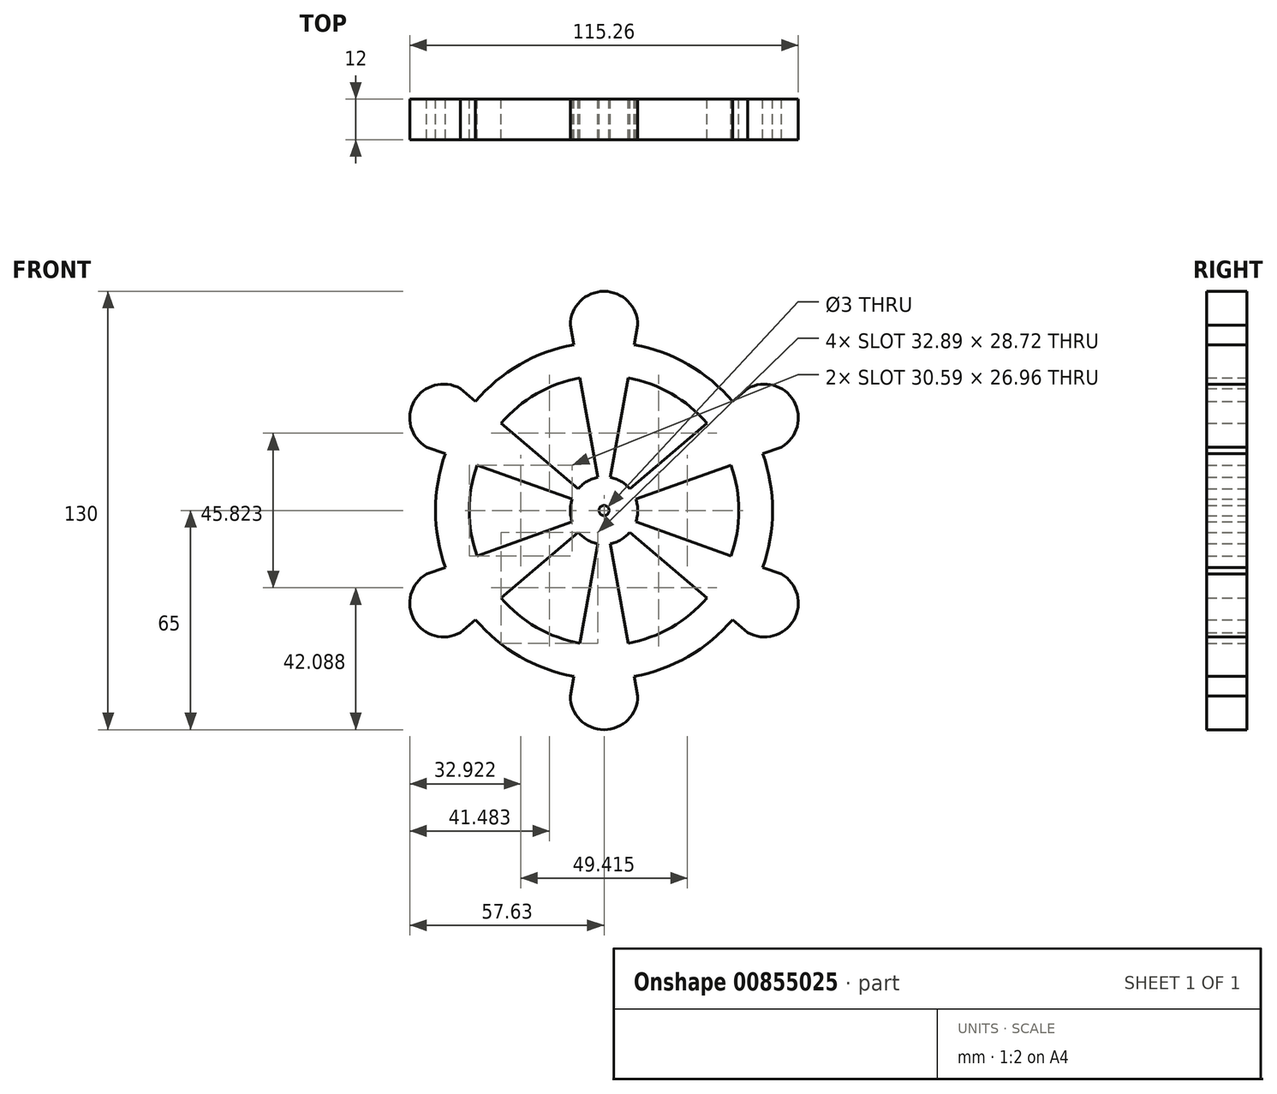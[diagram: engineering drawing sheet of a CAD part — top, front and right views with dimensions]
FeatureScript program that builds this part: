
annotation { "Feature Type Name" : "Feature", "Feature Type Description" : "" }
export const myFeature = defineFeature(function(context is Context, id is Id, definition is map)
    precondition{}
    {
        {
            var Q0;
            Q0=qCreatedBy(makeId("Front.planeOp"),FACE);
            var sketch = newSketch(context, id + "F0", { "sketchPlane" : qUnion([Q0])});
            skArc(sketch, "E0", {"start": v(-0.9, 4.92) * mm, "mid": v(-2.5, 4.33) * mm, "end": v(-3.81, 3.23) * mm});
            skArc(sketch, "E1", {"start": v(-0.72, 3.94) * mm, "mid": v(-2, 3.46) * mm, "end": v(-3.05, 2.59) * mm});
            skCircle(sketch, "E2", {"center": v(0, 0) * mm, "radius": 1 * mm});
            skLineSegment(sketch, "E3", {"start": v(-0.18, 0.98) * mm, "end": v(-1, 5.5) * mm});
            skLineSegment(sketch, "E4", {"start": v(0.18, 0.98) * mm, "end": v(1, 5.5) * mm});
            skArc(sketch, "E5", {"start": v(1, 5.5) * mm, "mid": v(0, 6.5) * mm, "end": v(-1, 5.5) * mm});
            skArc(sketch, "E6.1.0", {"start": v(-4.26, 3.62) * mm, "mid": v(-5.63, 3.25) * mm, "end": v(-5.26, 1.88) * mm});
            skLineSegment(sketch, "E6.1.1", {"start": v(-0.76, 0.65) * mm, "end": v(-4.26, 3.62) * mm});
            skLineSegment(sketch, "E6.1.2", {"start": v(-0.94, 0.34) * mm, "end": v(-5.26, 1.88) * mm});
            skArc(sketch, "E6.2.0", {"start": v(-5.26, -1.88) * mm, "mid": v(-5.63, -3.25) * mm, "end": v(-4.26, -3.62) * mm});
            skLineSegment(sketch, "E6.2.1", {"start": v(-0.94, -0.34) * mm, "end": v(-5.26, -1.88) * mm});
            skLineSegment(sketch, "E6.2.2", {"start": v(-0.76, -0.65) * mm, "end": v(-4.26, -3.62) * mm});
            skArc(sketch, "E6.3.0", {"start": v(-1, -5.5) * mm, "mid": v(0, -6.5) * mm, "end": v(1, -5.5) * mm});
            skLineSegment(sketch, "E6.3.1", {"start": v(-0.18, -0.98) * mm, "end": v(-1, -5.5) * mm});
            skLineSegment(sketch, "E6.3.2", {"start": v(0.18, -0.98) * mm, "end": v(1, -5.5) * mm});
            skArc(sketch, "E6.4.0", {"start": v(4.26, -3.62) * mm, "mid": v(5.63, -3.25) * mm, "end": v(5.26, -1.88) * mm});
            skLineSegment(sketch, "E6.4.1", {"start": v(0.76, -0.65) * mm, "end": v(4.26, -3.62) * mm});
            skLineSegment(sketch, "E6.4.2", {"start": v(0.94, -0.34) * mm, "end": v(5.26, -1.88) * mm});
            skArc(sketch, "E6.5.0", {"start": v(5.26, 1.88) * mm, "mid": v(5.63, 3.25) * mm, "end": v(4.26, 3.62) * mm});
            skLineSegment(sketch, "E6.5.1", {"start": v(0.94, 0.34) * mm, "end": v(5.26, 1.88) * mm});
            skLineSegment(sketch, "E6.5.2", {"start": v(0.76, 0.65) * mm, "end": v(4.26, 3.62) * mm});
            skArc(sketch, "E7.trimOffspring", {"start": v(-4.7, 1.69) * mm, "mid": v(-5, 0) * mm, "end": v(-4.7, -1.69) * mm});
            skArc(sketch, "E8.trimOffspring", {"start": v(-3.77, 1.35) * mm, "mid": v(-4, 0) * mm, "end": v(-3.77, -1.35) * mm});
            skArc(sketch, "E9.trimOffspring", {"start": v(-3.81, -3.23) * mm, "mid": v(-2.5, -4.33) * mm, "end": v(-0.9, -4.92) * mm});
            skArc(sketch, "E10.trimOffspring", {"start": v(-3.05, -2.59) * mm, "mid": v(-2, -3.46) * mm, "end": v(-0.72, -3.94) * mm});
            skArc(sketch, "E11.trimOffspring", {"start": v(0.72, -3.94) * mm, "mid": v(2, -3.46) * mm, "end": v(3.05, -2.59) * mm});
            skArc(sketch, "E12.trimOffspring", {"start": v(0.9, -4.92) * mm, "mid": v(2.5, -4.33) * mm, "end": v(3.81, -3.23) * mm});
            skArc(sketch, "E13.trimOffspring", {"start": v(4.7, -1.69) * mm, "mid": v(5, 0) * mm, "end": v(4.7, 1.69) * mm});
            skArc(sketch, "E14.trimOffspring", {"start": v(3.77, -1.35) * mm, "mid": v(4, 0) * mm, "end": v(3.77, 1.35) * mm});
            skArc(sketch, "E15.trimOffspring", {"start": v(3.05, 2.59) * mm, "mid": v(2, 3.46) * mm, "end": v(0.72, 3.94) * mm});
            skArc(sketch, "E16.trimOffspring", {"start": v(3.81, 3.23) * mm, "mid": v(2.5, 4.33) * mm, "end": v(0.9, 4.92) * mm});
            skSolve(sketch);
        }
        {
            var Q0;
            {var subQ0=sQuery(id+"F0.wireOp",EDGE,"E7.trimOffspring");Q0=makeQuery(id+"F0.imprint","IMPRINT",FACE,{"disambiguationData":[TD([[makeQuery(id+"F0.imprint","IMPRINT",EDGE,{"derivedFrom":subQ0}),1.0]])]});}
            var Q1;
            {var subQ5=sQuery(id+"F0.wireOp",EDGE,"E6.1.0");Q1=makeQuery(id+"F0.imprint","IMPRINT",FACE,{"disambiguationData":[TD([[makeQuery(id+"F0.imprint","IMPRINT",EDGE,{"derivedFrom":subQ5}),1.0]])]});}
            var Q2;
            {var subQ0=sQuery(id+"F0.wireOp",EDGE,"E0");Q2=makeQuery(id+"F0.imprint","IMPRINT",FACE,{"disambiguationData":[TD([[makeQuery(id+"F0.imprint","IMPRINT",EDGE,{"derivedFrom":subQ0}),1.0]])]});}
            var Q3;
            {var subQ2=sQuery(id+"F0.wireOp",EDGE,"E5");Q3=makeQuery(id+"F0.imprint","IMPRINT",FACE,{"disambiguationData":[TD([[makeQuery(id+"F0.imprint","IMPRINT",EDGE,{"derivedFrom":subQ2}),1.0]])]});}
            var Q4;
            {var subQ0=sQuery(id+"F0.wireOp",EDGE,"E15.trimOffspring");Q4=makeQuery(id+"F0.imprint","IMPRINT",FACE,{"disambiguationData":[TD([[makeQuery(id+"F0.imprint","IMPRINT",EDGE,{"derivedFrom":subQ0}),-1.0]])]});}
            var Q5;
            {var subQ5=sQuery(id+"F0.wireOp",EDGE,"E6.5.0");Q5=makeQuery(id+"F0.imprint","IMPRINT",FACE,{"disambiguationData":[TD([[makeQuery(id+"F0.imprint","IMPRINT",EDGE,{"derivedFrom":subQ5}),1.0]])]});}
            var Q6;
            {var subQ0=sQuery(id+"F0.wireOp",EDGE,"E13.trimOffspring");Q6=makeQuery(id+"F0.imprint","IMPRINT",FACE,{"disambiguationData":[TD([[makeQuery(id+"F0.imprint","IMPRINT",EDGE,{"derivedFrom":subQ0}),1.0]])]});}
            var Q7;
            {var subQ5=sQuery(id+"F0.wireOp",EDGE,"E6.4.0");Q7=makeQuery(id+"F0.imprint","IMPRINT",FACE,{"disambiguationData":[TD([[makeQuery(id+"F0.imprint","IMPRINT",EDGE,{"derivedFrom":subQ5}),1.0]])]});}
            var Q8;
            {var subQ0=sQuery(id+"F0.wireOp",EDGE,"E11.trimOffspring");Q8=makeQuery(id+"F0.imprint","IMPRINT",FACE,{"disambiguationData":[TD([[makeQuery(id+"F0.imprint","IMPRINT",EDGE,{"derivedFrom":subQ0}),-1.0]])]});}
            var Q9;
            {var subQ5=sQuery(id+"F0.wireOp",EDGE,"E6.3.0");Q9=makeQuery(id+"F0.imprint","IMPRINT",FACE,{"disambiguationData":[TD([[makeQuery(id+"F0.imprint","IMPRINT",EDGE,{"derivedFrom":subQ5}),1.0]])]});}
            var Q10;
            {var subQ7=sQuery(id+"F0.wireOp",EDGE,"E6.2.0");Q10=makeQuery(id+"F0.imprint","IMPRINT",FACE,{"disambiguationData":[TD([[makeQuery(id+"F0.imprint","IMPRINT",EDGE,{"derivedFrom":subQ7}),1.0]])]});}
            var Q11;
            {var subQ0=sQuery(id+"F0.wireOp",EDGE,"E2");var subQ8=makeQuery(id+"F0.imprint","INTERSECT",VERTEX,{"derivedFrom":[subQ0,sQuery(id+"F0.wireOp",EDGE,"E6.5.1")]});Q11=makeQuery(id+"F0.imprint","IMPRINT",FACE,{"disambiguationData":[TD([[makeQuery(id+"F0.imprint","IMPRINT",EDGE,{"disambiguationData":[TD([[subQ8,-1.0]])],"derivedFrom":subQ0}),1.0]])]});}
            var Q12;
            {var subQ0=sQuery(id+"F0.wireOp",EDGE,"E9.trimOffspring");Q12=makeQuery(id+"F0.imprint","IMPRINT",FACE,{"disambiguationData":[TD([[makeQuery(id+"F0.imprint","IMPRINT",EDGE,{"derivedFrom":subQ0}),1.0]])]});}
            extrude(context, id + "F1", {"entities" : qUnion([Q0, Q1, Q2, Q3, Q4, Q5, Q6, Q7, Q8, Q9, Q10, Q11, Q12]), "depth" : 1.2 * mm, "offsetDistance" : 25 * mm});
        }
        {
            var Q0;
            Q0=makeQuery(id+"F1.opExtrude","SWEPT_BODY",BODY,{"disambiguationData":[OSD([sQuery(id+"F0.wireOp",EDGE,"E0"),sQuery(id+"F0.wireOp",EDGE,"E1"),sQuery(id+"F0.wireOp",EDGE,"E2"),sQuery(id+"F0.wireOp",EDGE,"E3"),sQuery(id+"F0.wireOp",EDGE,"E4"),sQuery(id+"F0.wireOp",EDGE,"E5"),sQuery(id+"F0.wireOp",EDGE,"E6.1.0"),sQuery(id+"F0.wireOp",EDGE,"E6.1.1"),sQuery(id+"F0.wireOp",EDGE,"E6.1.2"),sQuery(id+"F0.wireOp",EDGE,"E6.2.0"),sQuery(id+"F0.wireOp",EDGE,"E6.2.1"),sQuery(id+"F0.wireOp",EDGE,"E6.2.2"),sQuery(id+"F0.wireOp",EDGE,"E6.3.0"),sQuery(id+"F0.wireOp",EDGE,"E6.3.1"),sQuery(id+"F0.wireOp",EDGE,"E6.3.2"),sQuery(id+"F0.wireOp",EDGE,"E6.4.0"),sQuery(id+"F0.wireOp",EDGE,"E6.4.1"),sQuery(id+"F0.wireOp",EDGE,"E6.4.2"),sQuery(id+"F0.wireOp",EDGE,"E6.5.0"),sQuery(id+"F0.wireOp",EDGE,"E6.5.1"),sQuery(id+"F0.wireOp",EDGE,"E6.5.2"),sQuery(id+"F0.wireOp",EDGE,"E7.trimOffspring"),sQuery(id+"F0.wireOp",EDGE,"E8.trimOffspring"),sQuery(id+"F0.wireOp",EDGE,"E9.trimOffspring"),sQuery(id+"F0.wireOp",EDGE,"E10.trimOffspring"),sQuery(id+"F0.wireOp",EDGE,"E11.trimOffspring"),sQuery(id+"F0.wireOp",EDGE,"E12.trimOffspring"),sQuery(id+"F0.wireOp",EDGE,"E13.trimOffspring"),sQuery(id+"F0.wireOp",EDGE,"E14.trimOffspring"),sQuery(id+"F0.wireOp",EDGE,"E15.trimOffspring"),sQuery(id+"F0.wireOp",EDGE,"E16.trimOffspring")])]});
            var Q1;
            Q1=qCreatedBy(makeId("Origin.pointOp"),VERTEX);
            transform(context, id + "F2", {"entities" : qUnion([Q0]), "transformType" : TransformType.SCALE_UNIFORMLY, "scale" : 10, "scalePoint" : qUnion([Q1]), "makeCopy" : false});
        }
        {
            var Q0;
            Q0=qCreatedBy(makeId("Front.planeOp"),FACE);
            var sketch = newSketch(context, id + "F3", { "sketchPlane" : qUnion([Q0])});
            skCircle(sketch, "E17", {"center": v(0, 0) * mm, "radius": 1.5 * mm});
            skSolve(sketch);
        }
        {
            var Q0;
            Q0=sQuery(id+"F3.wireOp",VERTEX,"E17.center");
            var Q1;
            Q1=makeQuery(id+"F1.opExtrude","SWEPT_BODY",BODY,{"disambiguationData":[OSD([sQuery(id+"F0.wireOp",EDGE,"E0"),sQuery(id+"F0.wireOp",EDGE,"E1"),sQuery(id+"F0.wireOp",EDGE,"E2"),sQuery(id+"F0.wireOp",EDGE,"E3"),sQuery(id+"F0.wireOp",EDGE,"E4"),sQuery(id+"F0.wireOp",EDGE,"E5"),sQuery(id+"F0.wireOp",EDGE,"E6.1.0"),sQuery(id+"F0.wireOp",EDGE,"E6.1.1"),sQuery(id+"F0.wireOp",EDGE,"E6.1.2"),sQuery(id+"F0.wireOp",EDGE,"E6.2.0"),sQuery(id+"F0.wireOp",EDGE,"E6.2.1"),sQuery(id+"F0.wireOp",EDGE,"E6.2.2"),sQuery(id+"F0.wireOp",EDGE,"E6.3.0"),sQuery(id+"F0.wireOp",EDGE,"E6.3.1"),sQuery(id+"F0.wireOp",EDGE,"E6.3.2"),sQuery(id+"F0.wireOp",EDGE,"E6.4.0"),sQuery(id+"F0.wireOp",EDGE,"E6.4.1"),sQuery(id+"F0.wireOp",EDGE,"E6.4.2"),sQuery(id+"F0.wireOp",EDGE,"E6.5.0"),sQuery(id+"F0.wireOp",EDGE,"E6.5.1"),sQuery(id+"F0.wireOp",EDGE,"E6.5.2"),sQuery(id+"F0.wireOp",EDGE,"E7.trimOffspring"),sQuery(id+"F0.wireOp",EDGE,"E8.trimOffspring"),sQuery(id+"F0.wireOp",EDGE,"E9.trimOffspring"),sQuery(id+"F0.wireOp",EDGE,"E10.trimOffspring"),sQuery(id+"F0.wireOp",EDGE,"E11.trimOffspring"),sQuery(id+"F0.wireOp",EDGE,"E12.trimOffspring"),sQuery(id+"F0.wireOp",EDGE,"E13.trimOffspring"),sQuery(id+"F0.wireOp",EDGE,"E14.trimOffspring"),sQuery(id+"F0.wireOp",EDGE,"E15.trimOffspring"),sQuery(id+"F0.wireOp",EDGE,"E16.trimOffspring")])]});
            hole(context, id + "F4", {"style" : HoleStyle.SIMPLE, "endStyle" : HoleEndStyle.THROUGH, "oppositeDirection" : true, "holeDiameter" : 3 * mm, "majorDiameter" : 5 * mm, "isTappedThrough" : true, "tappedDepth" : 12 * mm, "tapClearance" : 3, "locations" : qUnion([Q0]), "scope" : qUnion([Q1])});
        }
    });
